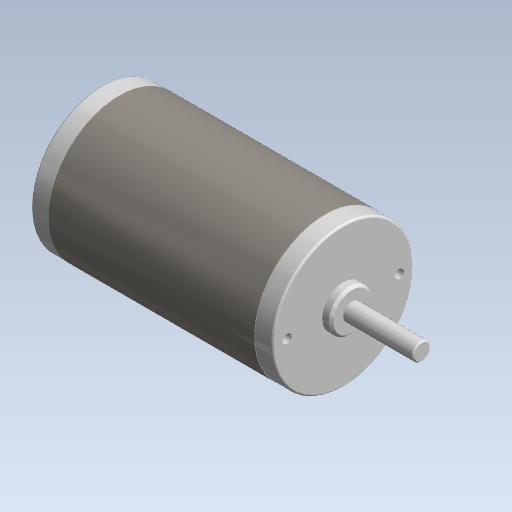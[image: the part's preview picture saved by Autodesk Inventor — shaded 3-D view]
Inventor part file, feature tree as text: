
AUTODESK INVENTOR PART (.ipt)
format: ipt  version: 2020 (Build 240168000, 168)  size: 137,216 bytes
history: native  units: mm (DEFAULTED — no unit token found)
features: chamfer x1
ambient origin geometry x8: Origin, YZ Plane, XZ Plane, XY Plane, X Axis, Y Axis, Z Axis, Center Point
bodies: Solid1 (feature_tree)
feature tree (1):
  chamfer  "Chamfer3"  [1 undecoded]
note: 1 required parameter value undecoded (feature->parameter linkage not recoverable at this tier; creation-order binding heuristic only, values carry confidence <= 0.55)
